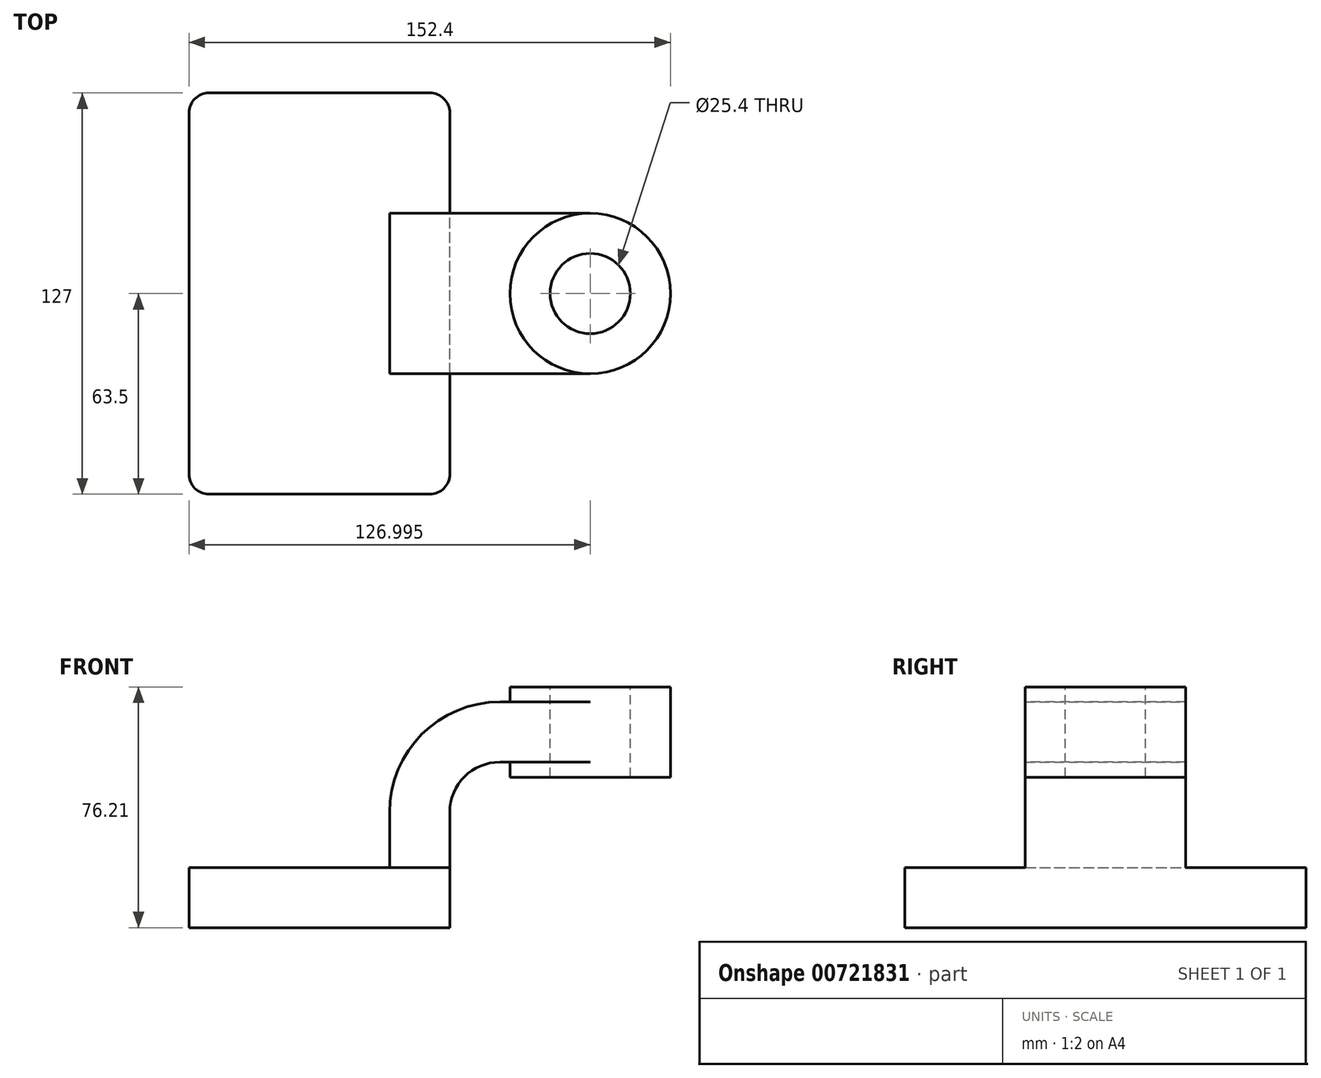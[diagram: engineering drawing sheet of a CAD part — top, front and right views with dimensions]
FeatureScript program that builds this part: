
annotation { "Feature Type Name" : "Feature", "Feature Type Description" : "" }
export const myFeature = defineFeature(function(context is Context, id is Id, definition is map)
    precondition{}
    {
        {
            var Q0;
            Q0=qCreatedBy(makeId("Front.planeOp"),FACE);
            var sketch = newSketch(context, id + "F0", { "sketchPlane" : qUnion([Q0])});
            skLineSegment(sketch, "E0.bottom", {"start": v(41.27, 9.53) * mm, "end": v(-41.28, 9.53) * mm});
            skLineSegment(sketch, "E0.top", {"start": v(41.28, -9.52) * mm, "end": v(-41.27, -9.52) * mm});
            skLineSegment(sketch, "E0.left", {"start": v(41.28, 9.53) * mm, "end": v(41.28, -9.52) * mm});
            skLineSegment(sketch, "E0.right", {"start": v(-41.28, 9.53) * mm, "end": v(-41.28, -9.52) * mm});
            skPoint(sketch, "E0.middle", {"position": v(0, 0) * mm});
            skLineSegment(sketch, "E1.bottom", {"start": v(111.12, 38.1) * mm, "end": v(60.32, 38.1) * mm});
            skLineSegment(sketch, "E1.top", {"start": v(111.12, 66.68) * mm, "end": v(60.32, 66.68) * mm});
            skLineSegment(sketch, "E1.left", {"start": v(111.12, 38.1) * mm, "end": v(111.12, 66.68) * mm});
            skLineSegment(sketch, "E1.right", {"start": v(60.32, 38.1) * mm, "end": v(60.32, 66.68) * mm});
            skPoint(sketch, "E1.middle", {"position": v(85.72, 52.39) * mm});
            skLineSegment(sketch, "E2", {"start": v(41.27, 9.53) * mm, "end": v(41.27, 27) * mm});
            skArc(sketch, "E3", {"start": v(41.27, 27) * mm, "mid": v(45.92, 38.23) * mm, "end": v(57.15, 42.88) * mm});
            skLineSegment(sketch, "E4", {"start": v(57.15, 42.88) * mm, "end": v(85.72, 42.88) * mm});
            skLineSegment(sketch, "E5.0", {"start": v(57.15, 61.93) * mm, "end": v(85.72, 61.93) * mm});
            skArc(sketch, "E5.1", {"start": v(22.22, 27) * mm, "mid": v(32.45, 51.7) * mm, "end": v(57.15, 61.93) * mm});
            skLineSegment(sketch, "E5.2", {"start": v(22.22, 9.53) * mm, "end": v(22.22, 27) * mm});
            skLineSegment(sketch, "E6", {"start": v(85.72, 61.93) * mm, "end": v(85.72, 42.88) * mm});
            skLineSegment(sketch, "E7", {"start": v(85.72, 66.68) * mm, "end": v(85.72, 61.93) * mm});
            skFitSpline(sketch, "E8", {"points": [v(-41.28, 9.53) * mm, v(57.15, 61.93) * mm], "startDerivative": vector(34.88, 56.76) * mm, "endDerivative": vector(208.85, -1.23) * mm});
            skLineSegment(sketch, "E9", {"start": v(85.72, 42.88) * mm, "end": v(85.72, 38.1) * mm});
            skSolve(sketch);
        }
        {
            var Q0;
            Q0=makeQuery(id+"F0.imprint","IMPRINT",FACE,{"disambiguationData":[TD([[makeQuery(id+"F0.imprint","IMPRINT",EDGE,{"derivedFrom":sQuery(id+"F0.wireOp",EDGE,"E0.top")}),-1.0]])]});
            extrude(context, id + "F1", {"entities" : qUnion([Q0]), "endBound" : BoundingType.SYMMETRIC, "depth" : 127 * mm, "offsetDistance" : 25.4 * mm});
        }
        {
            var Q0;
            {var subQ1=sQuery(id+"F0.wireOp",EDGE,"E2");Q0=makeQuery(id+"F0.imprint","IMPRINT",FACE,{"disambiguationData":[TD([[makeQuery(id+"F0.imprint","IMPRINT",EDGE,{"derivedFrom":subQ1}),1.0]])]});}
            var Q1;
            {var subQ5=sQuery(id+"F0.wireOp",EDGE,"E6");Q1=makeQuery(id+"F0.imprint","IMPRINT",FACE,{"disambiguationData":[TD([[makeQuery(id+"F0.imprint","IMPRINT",EDGE,{"derivedFrom":subQ5}),-1.0]])]});}
            extrude(context, id + "F2", {"entities" : qUnion([Q0, Q1]), "operationType" : NewBodyOperationType.ADD, "endBound" : BoundingType.SYMMETRIC, "depth" : 50.8 * mm, "offsetDistance" : 25.4 * mm});
        }
        {
            var Q0;
            Q0=makeQuery(id+"F0.imprint","IMPRINT",FACE,{"disambiguationData":[TD([[makeQuery(id+"F0.imprint","IMPRINT",EDGE,{"derivedFrom":sQuery(id+"F0.wireOp",EDGE,"E5.1")}),1.0]])]});
            extrude(context, id + "F3", {"entities" : qUnion([Q0]), "operationType" : NewBodyOperationType.ADD, "endBound" : BoundingType.SYMMETRIC, "depth" : 15.88 * mm, "offsetDistance" : 25.4 * mm});
        }
        {
            var Q0;
            {var subQ0=sQuery(id+"F0.wireOp",EDGE,"E1.left");Q0=makeQuery(id+"F0.imprint","IMPRINT",FACE,{"disambiguationData":[TD([[makeQuery(id+"F0.imprint","IMPRINT",EDGE,{"derivedFrom":subQ0}),1.0]])]});}
            var Q1;
            Q1=sQuery(id+"F0.wireOp",EDGE,"E6");
            revolve(context, id + "F4", {"operationType" : NewBodyOperationType.ADD, "surfaceOperationType" : NewSurfaceOperationType.NEW, "entities" : qUnion([Q0]), "axis" : qUnion([Q1]), "revolveType" : RevolveType.FULL});
        }
        {
            var Q0;
            Q0=makeQuery(id+"F1.opExtrude","CAP_EDGE",EDGE,{"disambiguationData":[OSD([sQuery(id+"F0.wireOp",EDGE,"E0.left")])],"isStart":false});
            var Q1;
            Q1=makeQuery(id+"F1.opExtrude","CAP_EDGE",EDGE,{"disambiguationData":[OSD([sQuery(id+"F0.wireOp",EDGE,"E0.right")])],"isStart":false});
            var Q2;
            Q2=makeQuery(id+"F1.opExtrude","CAP_EDGE",EDGE,{"disambiguationData":[OSD([sQuery(id+"F0.wireOp",EDGE,"E0.right")])],"isStart":true});
            var Q3;
            Q3=makeQuery(id+"F1.opExtrude","CAP_EDGE",EDGE,{"disambiguationData":[OSD([sQuery(id+"F0.wireOp",EDGE,"E0.left")])],"isStart":true});
            fillet(context, id + "F5", {"entities" : qUnion([Q0, Q1, Q2, Q3]), "radius" : 6.35 * mm, "tangentPropagation" : true, "allowEdgeOverflow" : false});
        }
        {
            var Q0;
            Q0=makeQuery(id+"F4.opRevolve","SWEPT_FACE",FACE,{"disambiguationData":[OSD([sQuery(id+"F0.wireOp",EDGE,"E1.top")])]});
            var sketch = newSketch(context, id + "F6", { "sketchPlane" : qUnion([Q0])});
            skCircle(sketch, "E10", {"center": v(85.72, 0) * mm, "radius": 12.7 * mm});
            skSolve(sketch);
        }
        {
            var Q0;
            Q0=makeQuery(id+"F6.imprint","IMPRINT",FACE,{"disambiguationData":[TD([[makeQuery(id+"F6.imprint","IMPRINT",EDGE,{"derivedFrom":sQuery(id+"F6.wireOp",EDGE,"E10")}),1.0]])]});
            extrude(context, id + "F7", {"entities" : qUnion([Q0]), "operationType" : NewBodyOperationType.REMOVE, "endBound" : BoundingType.THROUGH_ALL, "oppositeDirection" : true, "depth" : 25.4 * mm, "offsetDistance" : 25.4 * mm});
        }
    });
